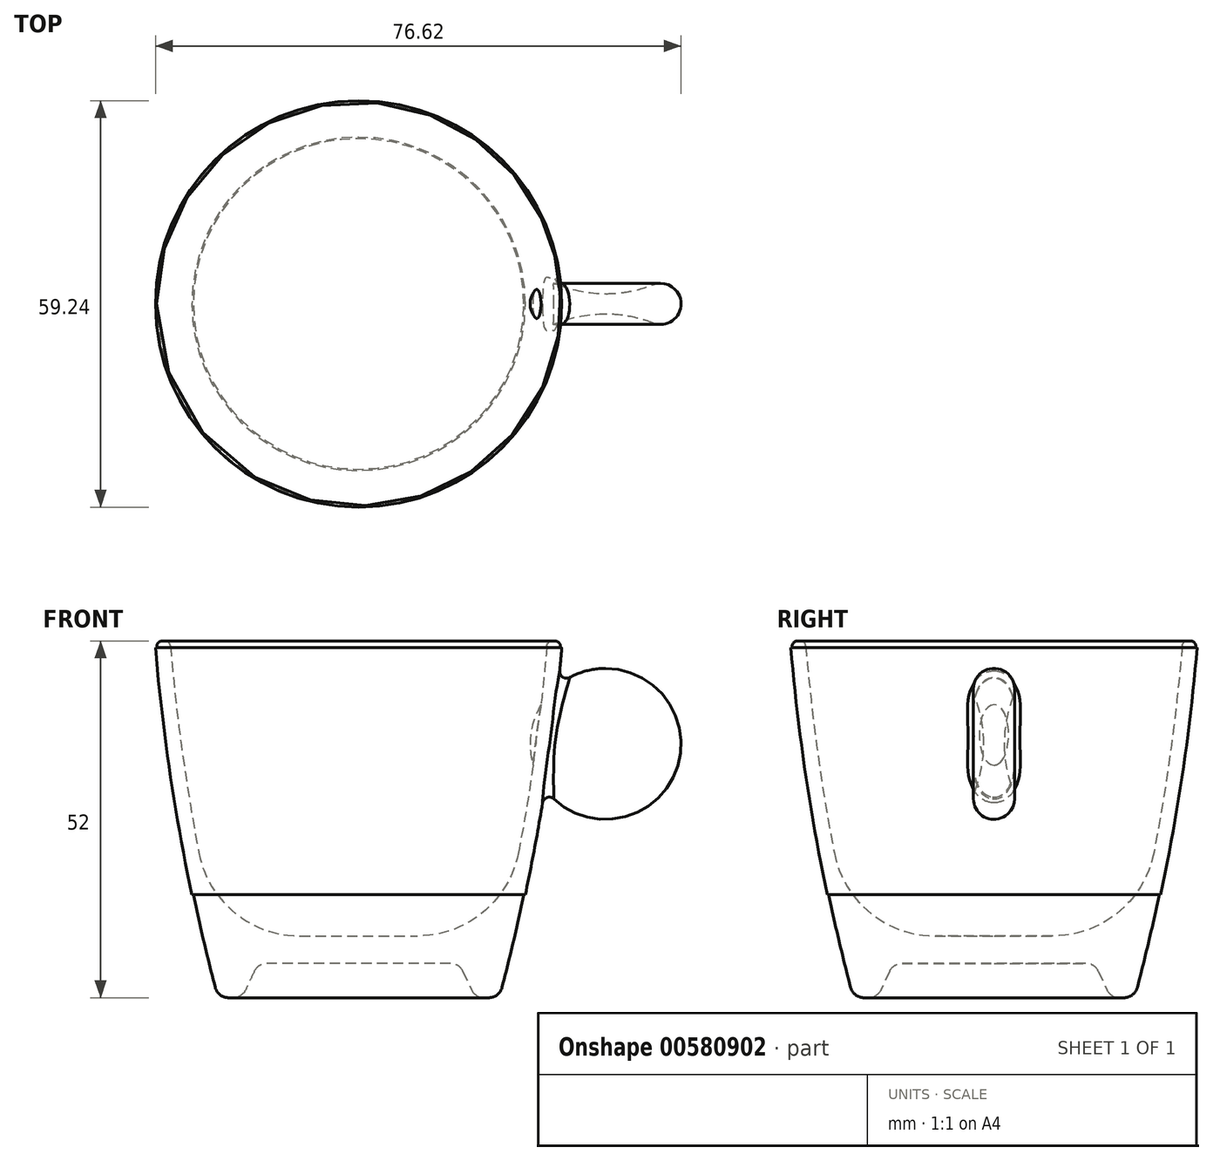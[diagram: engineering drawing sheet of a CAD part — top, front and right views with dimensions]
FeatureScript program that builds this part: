
annotation { "Feature Type Name" : "Feature", "Feature Type Description" : "" }
export const myFeature = defineFeature(function(context is Context, id is Id, definition is map)
    precondition{}
    {
        {
            var Q0;
            Q0=qCreatedBy(makeId("Front.planeOp"),FACE);
            var sketch = newSketch(context, id + "F0", { "sketchPlane" : qUnion([Q0])});
            skLineSegment(sketch, "E0", {"start": v(0, 5) * mm, "end": v(14.67, 5) * mm});
            skLineSegment(sketch, "E1", {"start": v(14.67, 5) * mm, "end": v(17, 0) * mm});
            skLineSegment(sketch, "E2", {"start": v(17, 0) * mm, "end": v(20.5, 0) * mm});
            skArc(sketch, "E3", {"start": v(20.5, 0) * mm, "mid": v(26.17, 25.8) * mm, "end": v(29.5, 52) * mm});
            skLineSegment(sketch, "E4", {"start": v(29.5, 52) * mm, "end": v(27.5, 52) * mm});
            skLineSegment(sketch, "E5", {"start": v(0, 9) * mm, "end": v(0, 5) * mm});
            skLineSegment(sketch, "E6", {"start": v(20.7, 9) * mm, "end": v(0, 9) * mm});
            skArc(sketch, "E7.trimOffspring", {"start": v(20.7, 9) * mm, "mid": v(24.9, 30.37) * mm, "end": v(27.5, 52) * mm});
            skPoint(sketch, "E8.orphan", {"position": v(0, 52) * mm});
            skSolve(sketch);
        }
        {
            var Q0;
            Q0=qSketchRegion(id+"F0",true);
            var Q1;
            Q1=sQuery(id+"F0.wireOp",EDGE,"E5");
            revolve(context, id + "F1", {"entities" : qUnion([Q0]), "axis" : qUnion([Q1]), "revolveType" : RevolveType.FULL});
        }
        {
            var Q0;
            Q0=makeQuery(id+"F1.opRevolve","SWEPT_EDGE",EDGE,{"disambiguationData":[OSD([sQuery(id+"F0.wireOp",EDGE,"E4"),sQuery(id+"F0.wireOp",EDGE,"E7.trimOffspring")])]});
            var Q1;
            Q1=makeQuery(id+"F1.opRevolve","SWEPT_EDGE",EDGE,{"disambiguationData":[OSD([sQuery(id+"F0.wireOp",EDGE,"E3"),sQuery(id+"F0.wireOp",EDGE,"E4")])]});
            fillet(context, id + "F2", {"entities" : qUnion([Q0, Q1]), "radius" : .8 * mm, "tangentPropagation" : true, "allowEdgeOverflow" : false});
        }
        {
            var Q0;
            Q0=makeQuery(id+"F1.opRevolve","SWEPT_EDGE",EDGE,{"disambiguationData":[OSD([sQuery(id+"F0.wireOp",EDGE,"E2"),sQuery(id+"F0.wireOp",EDGE,"E3")])]});
            var Q1;
            Q1=makeQuery(id+"F1.opRevolve","SWEPT_EDGE",EDGE,{"disambiguationData":[OSD([sQuery(id+"F0.wireOp",EDGE,"E1"),sQuery(id+"F0.wireOp",EDGE,"E2")])]});
            var Q2;
            Q2=makeQuery(id+"F1.opRevolve","SWEPT_EDGE",EDGE,{"disambiguationData":[OSD([sQuery(id+"F0.wireOp",EDGE,"E0"),sQuery(id+"F0.wireOp",EDGE,"E1")])]});
            fillet(context, id + "F3", {"entities" : qUnion([Q0, Q1, Q2]), "radius" : 2 * mm, "tangentPropagation" : true, "allowEdgeOverflow" : false});
        }
        {
            var Q0;
            Q0=makeQuery(id+"F1.opRevolve","SWEPT_EDGE",EDGE,{"disambiguationData":[OSD([sQuery(id+"F0.wireOp",EDGE,"E6"),sQuery(id+"F0.wireOp",EDGE,"E7.trimOffspring")])]});
            fillet(context, id + "F4", {"entities" : qUnion([Q0]), "radius" : 15 * mm, "tangentPropagation" : true, "allowEdgeOverflow" : false});
        }
        {
            var Q0;
            Q0=qCreatedBy(makeId("Front.planeOp"),FACE);
            var sketch = newSketch(context, id + "F5", { "sketchPlane" : qUnion([Q0])});
            skArc(sketch, "E9", {"start": v(24.3, 15) * mm, "mid": v(27.52, 32.92) * mm, "end": v(29.62, 51) * mm});
            skLineSegment(sketch, "E10", {"start": v(29.62, 51) * mm, "end": v(29.42, 51) * mm});
            skLineSegment(sketch, "E11", {"start": v(24.3, 15) * mm, "end": v(24.1, 15) * mm});
            skArc(sketch, "E12", {"start": v(24.1, 15) * mm, "mid": v(27.31, 32.92) * mm, "end": v(29.42, 51) * mm});
            skSolve(sketch);
        }
        {
            var Q0;
            Q0=makeQuery(id+"F5.imprint","IMPRINT",FACE,{"disambiguationData":[TD([[makeQuery(id+"F5.imprint","IMPRINT",EDGE,{"derivedFrom":sQuery(id+"F5.wireOp",EDGE,"E9")}),1.0]])]});
            var Q1;
            Q1=makeQuery(id+"F1.opRevolve","SWEPT_FACE",FACE,{"disambiguationData":[OSD([sQuery(id+"F0.wireOp",EDGE,"E7.trimOffspring")])]});
            revolve(context, id + "F6", {"operationType" : NewBodyOperationType.ADD, "entities" : qUnion([Q0]), "axis" : qUnion([Q1]), "revolveType" : RevolveType.FULL});
        }
        {
            var Q0;
            Q0=makeQuery(id+"F1.opRevolve","SWEPT_FACE",FACE,{"disambiguationData":[OSD([sQuery(id+"F0.wireOp",EDGE,"E4")])]});
            cPlane(context, id + "F7", {"entities" : qUnion([Q0]), "cplaneType" : CPlaneType.OFFSET, "offset" : 15 * mm, "oppositeDirection" : true, "width" : 150 * mm, "height" : 150 * mm});
        }
        {
            var Q0;
            Q0=qCreatedBy(id+"F7.planeOp",FACE);
            var sketch = newSketch(context, id + "F8", { "sketchPlane" : qUnion([Q0])});
            skArc(sketch, "E13", {"start": v(47, 0) * mm, "mid": v(45.7, 2.48) * mm, "end": v(42.91, 2.8) * mm});
            skArc(sketch, "E14", {"start": v(36, 1.5) * mm, "mid": v(39.52, 1.83) * mm, "end": v(42.91, 2.8) * mm});
            skLineSegment(sketch, "E15", {"start": v(36, 1.5) * mm, "end": v(36, 0) * mm});
            skLineSegment(sketch, "E16", {"start": v(36, 0) * mm, "end": v(47, 0) * mm, "construction": true});
            skArc(sketch, "E17.MirrorCS", {"start": v(47, 0) * mm, "mid": v(45.7, -2.48) * mm, "end": v(42.91, -2.8) * mm});
            skArc(sketch, "E18.MirrorCS", {"start": v(36, -1.5) * mm, "mid": v(39.52, -1.83) * mm, "end": v(42.91, -2.8) * mm});
            skLineSegment(sketch, "E19.MirrorCS", {"start": v(36, -1.5) * mm, "end": v(36, 0) * mm});
            skSolve(sketch);
        }
        {
            var Q0;
            Q0=makeQuery(id+"F8.imprint","IMPRINT",FACE,{"disambiguationData":[TD([[makeQuery(id+"F8.imprint","IMPRINT",EDGE,{"derivedFrom":sQuery(id+"F8.wireOp",EDGE,"E13")}),1.0]])]});
            var Q1;
            Q1=sQuery(id+"F8.wireOp",EDGE,"E15");
            revolve(context, id + "F9", {"operationType" : NewBodyOperationType.ADD, "entities" : qUnion([Q0]), "axis" : qUnion([Q1]), "revolveType" : RevolveType.FULL});
        }
        {
            var Q0;
            Q0=makeQuery(id+"F9.boolean.opBoolean","INTERSECT",EDGE,{"derivedFrom":[makeQuery(id+"F6.opRevolve","SWEPT_FACE",FACE,{"disambiguationData":[OSD([sQuery(id+"F5.wireOp",EDGE,"E9")])]}),makeQuery(id+"F9.opRevolve","SWEPT_FACE",FACE,{"disambiguationData":[OSD([sQuery(id+"F8.wireOp",EDGE,"E13"),sQuery(id+"F8.wireOp",EDGE,"E17.MirrorCS")])]})]});
            fillet(context, id + "F10", {"entities" : qUnion([Q0]), "radius" : 1 * mm, "tangentPropagation" : true, "allowEdgeOverflow" : false});
        }
    });
